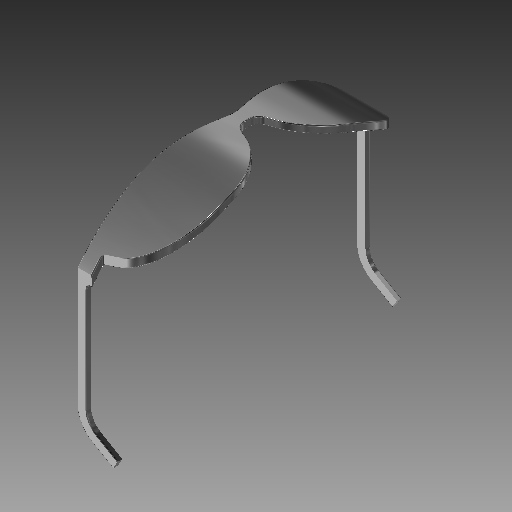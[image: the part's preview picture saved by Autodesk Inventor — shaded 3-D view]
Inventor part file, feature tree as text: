
AUTODESK INVENTOR PART (.ipt)
format: ipt  version: 2022 (Build 260153000, 153)  size: 577,024 bytes
history: native  units: mm (DEFAULTED — no unit token found)
features: fillet x4, extrude x3, sketch x3, mirror x2, other x1, projected_geometry x1
ambient origin geometry x8: Origin, YZ Plane, XZ Plane, XY Plane, X Axis, Y Axis, Z Axis, Center Point
bodies: Solid1 (feature_tree)
feature tree (14):
  other  "iMandy - 2D BODY"
  extrude  "Extrusion1"  Depth=10.0mm
  mirror  "Mirror1"
  extrude  "Extrusion2"  Depth=92.345631mm
  fillet  "Fillet1"  Radius=18.469126mm
  extrude  "Extrusion3"  Depth=0.79375mm
  fillet  "Fillet2"  Radius=4.7625mm
  mirror  "Mirror2"
  fillet  "Fillet3"  Radius=25.4mm
  fillet  "Fillet4"  Radius=18.469126mm
  sketch  "Sketch2"  dims[d1=10.0mm d17=6.35mm]
  sketch  "Sketch3"  dims[d18=48.019728mm d19=92.345631mm d20=18.469126mm]
  projected_geometry  "Projected Loop1"
  sketch  "Sketch4"  dims[d21=27.703689mm d22=92.345631mm d23=0.0mm d24=110.814757mm d25=4.7625mm d26=25.4mm d27=0.0mm d28=18.469126mm d29=6.002466mm d30=87.94822mm d31=30.0deg d32=3.175mm d33=0.0mm d34=19.05mm d35=1.5875mm d36=0.79375mm d37=26.384466mm d39=9.603946mm d40=1.745329mm d43=6.464194mm d55=12.7mm d56=37.455388mm d57=33.61381mm d58=15.0deg d59=8.382mm d60=177.8mm d62=92.345631mm d64=7.112mm d65=19.198622mm]
